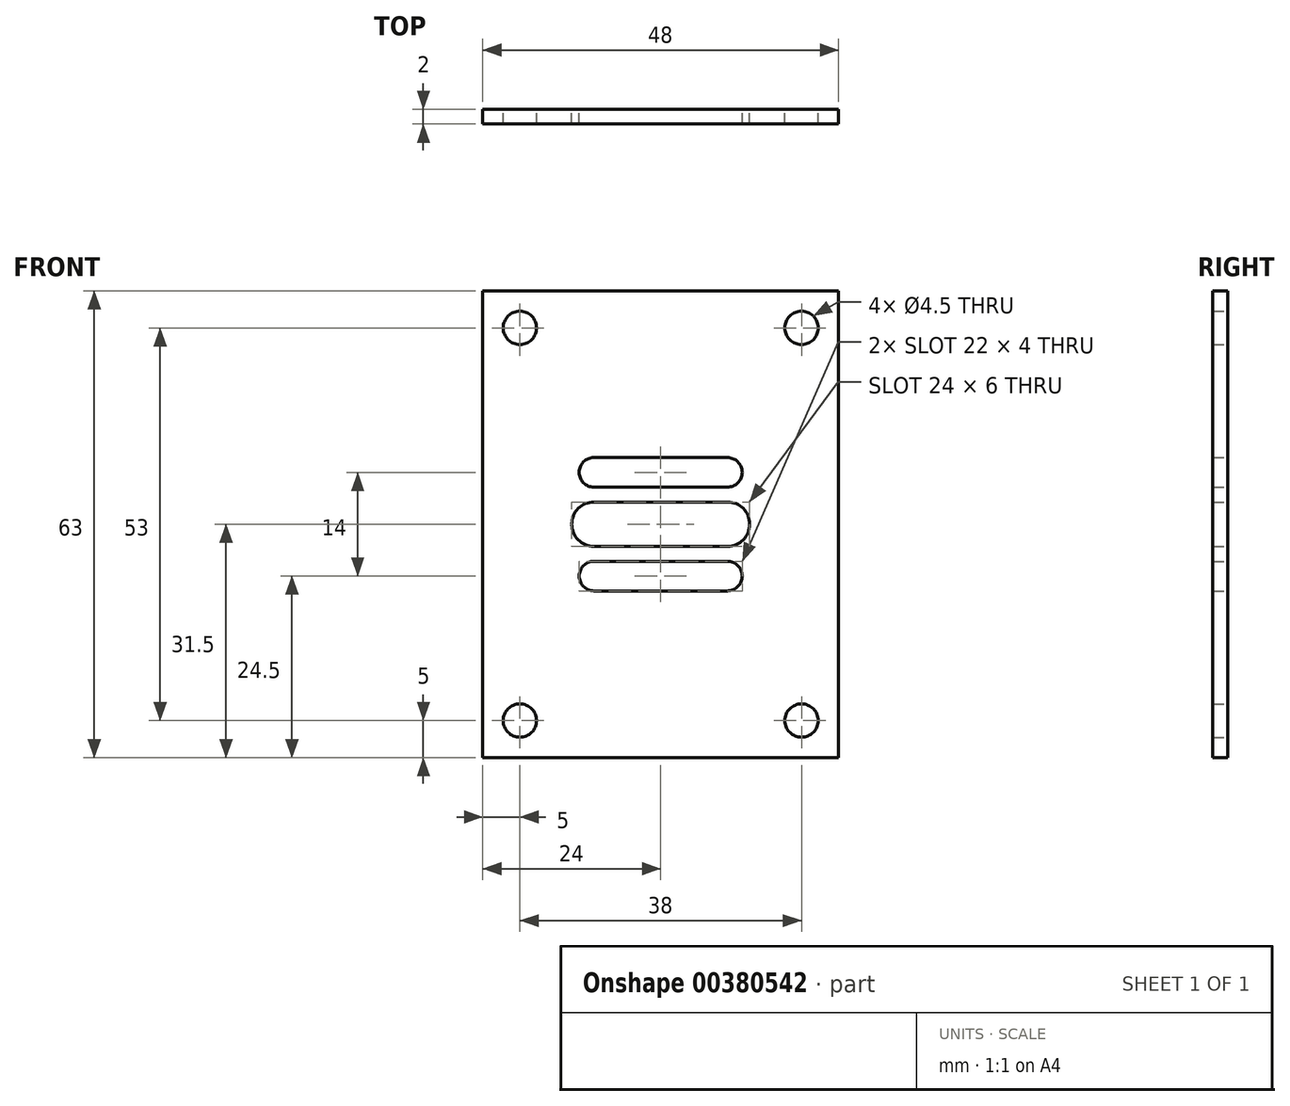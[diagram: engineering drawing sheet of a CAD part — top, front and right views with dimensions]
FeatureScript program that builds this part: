
annotation { "Feature Type Name" : "Feature", "Feature Type Description" : "" }
export const myFeature = defineFeature(function(context is Context, id is Id, definition is map)
    precondition{}
    {
        {
            var Q0;
            Q0=qCreatedBy(makeId("Front.planeOp"),FACE);
            var sketch = newSketch(context, id + "F0", { "sketchPlane" : qUnion([Q0])});
            skLineSegment(sketch, "E0.bottom", {"start": v(-24, 31.5) * mm, "end": v(24, 31.5) * mm});
            skLineSegment(sketch, "E0.top", {"start": v(-24, -31.5) * mm, "end": v(24, -31.5) * mm});
            skLineSegment(sketch, "E0.left", {"start": v(-24, 31.5) * mm, "end": v(-24, -31.5) * mm});
            skLineSegment(sketch, "E0.right", {"start": v(24, 31.5) * mm, "end": v(24, -31.5) * mm});
            skPoint(sketch, "E0.middle", {"position": v(0, 0) * mm});
            skLineSegment(sketch, "E1.bottom", {"start": v(-19, 26.5) * mm, "end": v(19, 26.5) * mm, "construction": true});
            skLineSegment(sketch, "E1.top", {"start": v(-19, -26.5) * mm, "end": v(19, -26.5) * mm, "construction": true});
            skLineSegment(sketch, "E1.left", {"start": v(-19, 26.5) * mm, "end": v(-19, -26.5) * mm, "construction": true});
            skLineSegment(sketch, "E1.right", {"start": v(19, 26.5) * mm, "end": v(19, -26.5) * mm, "construction": true});
            skCircle(sketch, "E2", {"center": v(-19, 26.5) * mm, "radius": 2.25 * mm});
            skCircle(sketch, "E3", {"center": v(19, 26.5) * mm, "radius": 2.25 * mm});
            skCircle(sketch, "E4", {"center": v(19, -26.5) * mm, "radius": 2.25 * mm});
            skCircle(sketch, "E5", {"center": v(-19, -26.5) * mm, "radius": 2.25 * mm});
            skLineSegment(sketch, "E6.bottom", {"start": v(9, 3) * mm, "end": v(-9, 3) * mm});
            skLineSegment(sketch, "E6.top", {"start": v(9, -3) * mm, "end": v(-9, -3) * mm});
            skLineSegment(sketch, "E6.left", {"start": v(9, 3) * mm, "end": v(9, -3) * mm, "construction": true});
            skLineSegment(sketch, "E6.right", {"start": v(-9, 3) * mm, "end": v(-9, -3) * mm, "construction": true});
            skLineSegment(sketch, "E7.bottom", {"start": v(9, 5) * mm, "end": v(-9, 5) * mm});
            skLineSegment(sketch, "E7.top", {"start": v(9, 9) * mm, "end": v(-9, 9) * mm});
            skLineSegment(sketch, "E7.left", {"start": v(9, 5) * mm, "end": v(9, 9) * mm, "construction": true});
            skLineSegment(sketch, "E7.right", {"start": v(-9, 5) * mm, "end": v(-9, 9) * mm, "construction": true});
            skPoint(sketch, "E7.middle", {"position": v(0, 7) * mm});
            skLineSegment(sketch, "E8.bottom", {"start": v(9, -9) * mm, "end": v(-9, -9) * mm});
            skLineSegment(sketch, "E8.top", {"start": v(9, -5) * mm, "end": v(-9, -5) * mm});
            skLineSegment(sketch, "E8.left", {"start": v(9, -9) * mm, "end": v(9, -5) * mm, "construction": true});
            skLineSegment(sketch, "E8.right", {"start": v(-9, -9) * mm, "end": v(-9, -5) * mm, "construction": true});
            skPoint(sketch, "E8.middle", {"position": v(0, -7) * mm});
            skPoint(sketch, "E9", {"position": v(0, -3) * mm});
            skLineSegment(sketch, "E10", {"start": v(0, 7) * mm, "end": v(0, -7) * mm, "construction": true});
            skArc(sketch, "E11", {"start": v(-9, 9) * mm, "mid": v(-11, 7) * mm, "end": v(-9, 5) * mm});
            skArc(sketch, "E12", {"start": v(9, 5) * mm, "mid": v(11, 7) * mm, "end": v(9, 9) * mm});
            skArc(sketch, "E13", {"start": v(9, -3) * mm, "mid": v(12, 0) * mm, "end": v(9, 3) * mm});
            skArc(sketch, "E14", {"start": v(-9, 3) * mm, "mid": v(-12, 0) * mm, "end": v(-9, -3) * mm});
            skArc(sketch, "E15", {"start": v(-9, -5) * mm, "mid": v(-11, -7) * mm, "end": v(-9, -9) * mm});
            skArc(sketch, "E16", {"start": v(9, -9) * mm, "mid": v(11, -7) * mm, "end": v(9, -5) * mm});
            skSolve(sketch);
        }
        {
            var Q0;
            Q0=makeQuery(id+"F0.imprint","IMPRINT",FACE,{"disambiguationData":[TD([[makeQuery(id+"F0.imprint","IMPRINT",EDGE,{"derivedFrom":sQuery(id+"F0.wireOp",EDGE,"E0.bottom")}),-1.0]])]});
            extrude(context, id + "F1", {"entities" : qUnion([Q0]), "depth" : 2 * mm});
        }
    });
